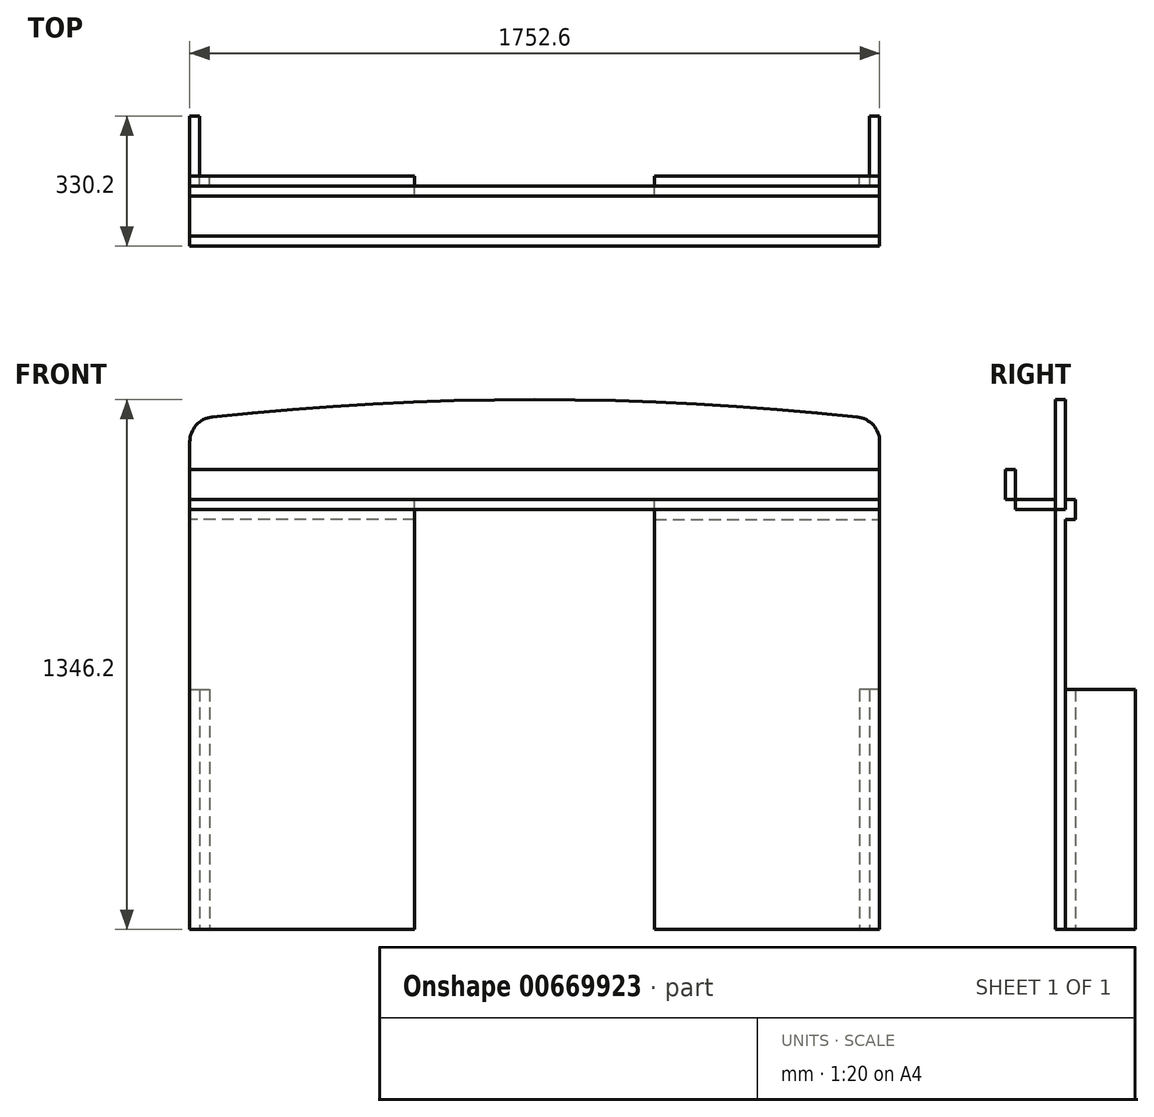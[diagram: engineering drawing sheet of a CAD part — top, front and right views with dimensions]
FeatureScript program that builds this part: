
annotation { "Feature Type Name" : "Feature", "Feature Type Description" : "" }
export const myFeature = defineFeature(function(context is Context, id is Id, definition is map)
    precondition{}
    {
        {
            var Q0;
            Q0=qCreatedBy(makeId("Top.planeOp"),FACE);
            var sketch = newSketch(context, id + "F0", { "sketchPlane" : qUnion([Q0])});
            skLineSegment(sketch, "E0.bottom", {"start": v(-876.3, 38.1) * mm, "end": v(876.3, 38.1) * mm, "construction": true});
            skLineSegment(sketch, "E0.top", {"start": v(-876.3, -38.1) * mm, "end": v(876.3, -38.1) * mm, "construction": true});
            skLineSegment(sketch, "E0.left", {"start": v(-876.3, 38.1) * mm, "end": v(-876.3, -38.1) * mm, "construction": true});
            skLineSegment(sketch, "E0.right", {"start": v(876.3, 38.1) * mm, "end": v(876.3, -38.1) * mm, "construction": true});
            skPoint(sketch, "E0.middle", {"position": v(0, 0) * mm});
            skLineSegment(sketch, "E1.bottom", {"start": v(-876.3, 38.1) * mm, "end": v(-850.9, 38.1) * mm});
            skLineSegment(sketch, "E1.top", {"start": v(-876.3, -139.7) * mm, "end": v(-850.9, -139.7) * mm});
            skLineSegment(sketch, "E1.left", {"start": v(-876.3, 38.1) * mm, "end": v(-876.3, -139.7) * mm});
            skLineSegment(sketch, "E1.right", {"start": v(-850.9, 38.1) * mm, "end": v(-850.9, -139.7) * mm});
            skSolve(sketch);
        }
        {
            var Q0;
            Q0 = qSketchRegion(id + "F0", true);
            extrude(context, id + "F1", {"entities" : qUnion([Q0]), "depth" : 609.6 * mm, "offsetDistance" : 25.4 * mm});
        }
        {
            var Q0;
            Q0=qCreatedBy(makeId("Top.planeOp"),FACE);
            var sketch = newSketch(context, id + "F2", { "sketchPlane" : qUnion([Q0])});
            skLineSegment(sketch, "E2.bottom", {"start": v(-850.9, -139.7) * mm, "end": v(-825.5, -139.7) * mm});
            skLineSegment(sketch, "E2.top", {"start": v(-850.9, -114.3) * mm, "end": v(-825.5, -114.3) * mm});
            skLineSegment(sketch, "E2.left", {"start": v(-850.9, -139.7) * mm, "end": v(-850.9, -114.3) * mm});
            skLineSegment(sketch, "E2.right", {"start": v(-825.5, -139.7) * mm, "end": v(-825.5, -114.3) * mm});
            skSolve(sketch);
        }
        {
            var Q0;
            Q0 = qSketchRegion(id + "F2", true);
            extrude(context, id + "F3", {"entities" : qUnion([Q0]), "depth" : 609.6 * mm, "offsetDistance" : 25.4 * mm});
        }
        {
            var Q0;
            Q0=makeQuery(id+"F1.opExtrude","SWEPT_FACE",FACE,{"disambiguationData":[OSD([sQuery(id+"F0.wireOp",EDGE,"E1.top")])]});
            var sketch = newSketch(context, id + "F4", { "sketchPlane" : qUnion([Q0])});
            skLineSegment(sketch, "E3", {"start": v(-876.3, 0) * mm, "end": v(-876.3, 1066.8) * mm});
            skLineSegment(sketch, "E4", {"start": v(-304.8, 1066.8) * mm, "end": v(-304.8, 0) * mm});
            skLineSegment(sketch, "E5", {"start": v(-304.8, 0) * mm, "end": v(-876.3, 0) * mm});
            skLineSegment(sketch, "E6", {"start": v(-876.3, 1066.8) * mm, "end": v(-304.8, 1066.8) * mm});
            skSolve(sketch);
        }
        {
            var Q0;
            Q0 = qSketchRegion(id + "F4", true);
            extrude(context, id + "F5", {"entities" : qUnion([Q0]), "depth" : 25.4 * mm, "offsetDistance" : 25.4 * mm});
        }
        {
            var Q0;
            Q0=makeQuery(id+"F5.opExtrude","CAP_FACE",FACE,{"disambiguationData":[OSD([sQuery(id+"F4.wireOp",EDGE,"E3"),sQuery(id+"F4.wireOp",EDGE,"E4"),sQuery(id+"F4.wireOp",EDGE,"E5"),sQuery(id+"F4.wireOp",EDGE,"E6")])],"isStart":true});
            var sketch = newSketch(context, id + "F6", { "sketchPlane" : qUnion([Q0])});
            skLineSegment(sketch, "E7", {"start": v(876.3, 1066.8) * mm, "end": v(876.3, 1295.4) * mm});
            skLineSegment(sketch, "E8", {"start": v(0, 0) * mm, "end": v(0, 1346.2) * mm, "construction": true});
            skArc(sketch, "E9", {"start": v(876.3, 1295.4) * mm, "mid": v(438.89, 1333.49) * mm, "end": v(0, 1346.2) * mm});
            skLineSegment(sketch, "E10", {"start": v(0, 1346.2) * mm, "end": v(-1371.48, 1346.2) * mm, "construction": true});
            skLineSegment(sketch, "E11", {"start": v(0, 1066.8) * mm, "end": v(0, 1346.2) * mm});
            skLineSegment(sketch, "E12", {"start": v(0, 1066.8) * mm, "end": v(304.8, 1066.8) * mm});
            skSolve(sketch);
        }
        {
            var Q0;
            Q0 = qSketchRegion(id + "F6", true);
            var Q1;
            Q1=makeQuery(id+"F6.imprint","IMPRINT",FACE,{"disambiguationData":[TD([[makeQuery(id+"F6.imprint","IMPRINT",EDGE,{"derivedFrom":sQuery(id+"F6.wireOp",EDGE,"E7")}),1.0]])]});
            extrude(context, id + "F7", {"entities" : qUnion([Q0, Q1]), "oppositeDirection" : true, "depth" : 25.4 * mm, "offsetDistance" : 25.4 * mm});
        }
        {
            var Q0;
            Q0=makeQuery(id+"F7.opExtrude","CAP_FACE",FACE,{"disambiguationData":[OSD([sQuery(id+"F4.wireOp",EDGE,"E6"),sQuery(id+"F6.wireOp",EDGE,"E7"),sQuery(id+"F6.wireOp",EDGE,"E9"),sQuery(id+"F6.wireOp",EDGE,"E11"),sQuery(id+"F6.wireOp",EDGE,"E12")])],"isStart":true});
            var sketch = newSketch(context, id + "F8", { "sketchPlane" : qUnion([Q0])});
            skLineSegment(sketch, "E13.bottom", {"start": v(304.8, 1041.4) * mm, "end": v(876.3, 1041.4) * mm});
            skLineSegment(sketch, "E13.top", {"start": v(304.8, 1092.2) * mm, "end": v(876.3, 1092.2) * mm});
            skLineSegment(sketch, "E13.left", {"start": v(304.8, 1041.4) * mm, "end": v(304.8, 1092.2) * mm});
            skLineSegment(sketch, "E13.right", {"start": v(876.3, 1041.4) * mm, "end": v(876.3, 1092.2) * mm});
            skPoint(sketch, "E13.middle", {"position": v(590.55, 1066.8) * mm});
            skSolve(sketch);
        }
        {
            var Q0;
            {var subQ0=sQuery(id+"F8.wireOp",EDGE,"E13.top");Q0=makeQuery(id+"F8.imprint","IMPRINT",FACE,{"disambiguationData":[TD([[makeQuery(id+"F8.imprint","IMPRINT",EDGE,{"derivedFrom":subQ0}),-1.0]])]});}
            var Q1;
            {var subQ0=sQuery(id+"F8.wireOp",EDGE,"E13.bottom");Q1=makeQuery(id+"F8.imprint","IMPRINT",FACE,{"disambiguationData":[TD([[makeQuery(id+"F8.imprint","IMPRINT",EDGE,{"derivedFrom":subQ0}),1.0]])]});}
            extrude(context, id + "F9", {"entities" : qUnion([Q0, Q1]), "depth" : 25.4 * mm, "offsetDistance" : 25.4 * mm});
        }
        {
            var Q0;
            Q0=makeQuery(id+"F7.opExtrude","SWEPT_BODY",BODY,{"disambiguationData":[OSD([sQuery(id+"F4.wireOp",EDGE,"E6"),sQuery(id+"F6.wireOp",EDGE,"E7"),sQuery(id+"F6.wireOp",EDGE,"E9"),sQuery(id+"F6.wireOp",EDGE,"E11"),sQuery(id+"F6.wireOp",EDGE,"E12")])]});
            var Q1;
            Q1=qCreatedBy(makeId("Right.planeOp"),FACE);
            mirror(context, id + "F10", {"operationType" : NewBodyOperationType.ADD, "entities" : qUnion([Q0]), "mirrorPlane" : qUnion([Q1])});
        }
        {
            var Q0;
            Q0=makeQuery(id+"F9.opExtrude","SWEPT_BODY",BODY,{"disambiguationData":[OSD([sQuery(id+"F8.wireOp",EDGE,"E13.bottom"),sQuery(id+"F8.wireOp",EDGE,"E13.top"),sQuery(id+"F8.wireOp",EDGE,"E13.left"),sQuery(id+"F8.wireOp",EDGE,"E13.right")])]});
            var Q1;
            Q1=makeQuery(id+"F5.opExtrude","SWEPT_BODY",BODY,{"disambiguationData":[OSD([sQuery(id+"F4.wireOp",EDGE,"E3"),sQuery(id+"F4.wireOp",EDGE,"E4"),sQuery(id+"F4.wireOp",EDGE,"E5"),sQuery(id+"F4.wireOp",EDGE,"E6")])]});
            var Q2;
            Q2=makeQuery(id+"F3.opExtrude","SWEPT_BODY",BODY,{"disambiguationData":[OSD([sQuery(id+"F2.wireOp",EDGE,"E2.bottom"),sQuery(id+"F2.wireOp",EDGE,"E2.top"),sQuery(id+"F2.wireOp",EDGE,"E2.left"),sQuery(id+"F2.wireOp",EDGE,"E2.right")])]});
            var Q3;
            Q3=makeQuery(id+"F1.opExtrude","SWEPT_BODY",BODY,{"disambiguationData":[OSD([sQuery(id+"F0.wireOp",EDGE,"E1.bottom"),sQuery(id+"F0.wireOp",EDGE,"E1.top"),sQuery(id+"F0.wireOp",EDGE,"E1.left"),sQuery(id+"F0.wireOp",EDGE,"E1.right")])]});
            var Q4;
            Q4=makeQuery(id+"F7.opExtrude","SWEPT_BODY",BODY,{"disambiguationData":[OSD([sQuery(id+"F4.wireOp",EDGE,"E6"),sQuery(id+"F6.wireOp",EDGE,"E7"),sQuery(id+"F6.wireOp",EDGE,"E9"),sQuery(id+"F6.wireOp",EDGE,"E11"),sQuery(id+"F6.wireOp",EDGE,"E12")])]});
            var Q5;
            Q5=qCreatedBy(makeId("Right.planeOp"),FACE);
            mirror(context, id + "F11", {"entities" : qUnion([Q0, Q1, Q2, Q3, Q4]), "mirrorPlane" : qUnion([Q5])});
        }
        {
            var Q0;
            Q0=makeQuery(id+"F7.opExtrude","SWEPT_EDGE",EDGE,{"disambiguationData":[OSD([sQuery(id+"F6.wireOp",EDGE,"E7"),sQuery(id+"F6.wireOp",EDGE,"E9")])]});
            var Q1;
            Q1=makeQuery(id+"F10.opPattern","COPY",EDGE,{"derivedFrom":makeQuery(id+"F7.opExtrude","SWEPT_EDGE",EDGE,{"disambiguationData":[OSD([sQuery(id+"F6.wireOp",EDGE,"E7"),sQuery(id+"F6.wireOp",EDGE,"E9")])]}),"instanceName":"1"});
            var Q2;
            Q2=makeQuery(id+"F11.opPattern","COPY",EDGE,{"derivedFrom":makeQuery(id+"F10.opPattern","COPY",EDGE,{"derivedFrom":makeQuery(id+"F7.opExtrude","SWEPT_EDGE",EDGE,{"disambiguationData":[OSD([sQuery(id+"F6.wireOp",EDGE,"E7"),sQuery(id+"F6.wireOp",EDGE,"E9")])]}),"instanceName":"1"}),"instanceName":"1"});
            var Q3;
            Q3=makeQuery(id+"F11.opPattern","COPY",EDGE,{"derivedFrom":makeQuery(id+"F7.opExtrude","SWEPT_EDGE",EDGE,{"disambiguationData":[OSD([sQuery(id+"F6.wireOp",EDGE,"E7"),sQuery(id+"F6.wireOp",EDGE,"E9")])]}),"instanceName":"1"});
            fillet(context, id + "F12", {"entities" : qUnion([Q0, Q1, Q2, Q3]), "radius" : 63.5 * mm, "tangentPropagation" : true, "allowEdgeOverflow" : false});
        }
        {
            var Q0;
            {var subQ0=makeQuery(id+"F7.opExtrude","CAP_FACE",FACE,{"disambiguationData":[OSD([sQuery(id+"F4.wireOp",EDGE,"E6"),sQuery(id+"F6.wireOp",EDGE,"E7"),sQuery(id+"F6.wireOp",EDGE,"E9"),sQuery(id+"F6.wireOp",EDGE,"E11"),sQuery(id+"F6.wireOp",EDGE,"E12")])],"isStart":false});Q0=makeQuery(id+"F10.boolean.opBoolean","MERGE",FACE,{"derivedFrom":[subQ0,makeQuery(id+"F10.opPattern","COPY",FACE,{"derivedFrom":subQ0,"instanceName":"1"})]});}
            var sketch = newSketch(context, id + "F13", { "sketchPlane" : qUnion([Q0])});
            skLineSegment(sketch, "E14.bottom", {"start": v(-876.3, 1066.8) * mm, "end": v(876.3, 1066.8) * mm});
            skLineSegment(sketch, "E14.top", {"start": v(-876.3, 1092.2) * mm, "end": v(876.3, 1092.2) * mm});
            skLineSegment(sketch, "E14.left", {"start": v(-876.3, 1066.8) * mm, "end": v(-876.3, 1092.2) * mm});
            skLineSegment(sketch, "E14.right", {"start": v(876.3, 1066.8) * mm, "end": v(876.3, 1092.2) * mm});
            skSolve(sketch);
        }
        {
            var Q0;
            Q0 = qSketchRegion(id + "F13", true);
            extrude(context, id + "F14", {"entities" : qUnion([Q0]), "depth" : 101.6 * mm, "offsetDistance" : 25.4 * mm});
        }
        {
            var Q0;
            Q0=makeQuery(id+"F14.opExtrude","CAP_FACE",FACE,{"disambiguationData":[OSD([sQuery(id+"F13.wireOp",EDGE,"E14.bottom"),sQuery(id+"F13.wireOp",EDGE,"E14.top"),sQuery(id+"F13.wireOp",EDGE,"E14.left"),sQuery(id+"F13.wireOp",EDGE,"E14.right")])],"isStart":false});
            var sketch = newSketch(context, id + "F15", { "sketchPlane" : qUnion([Q0])});
            skLineSegment(sketch, "E15.bottom", {"start": v(-876.3, 1066.8) * mm, "end": v(876.3, 1066.8) * mm});
            skLineSegment(sketch, "E15.top", {"start": v(-876.3, 1168.4) * mm, "end": v(876.3, 1168.4) * mm});
            skLineSegment(sketch, "E15.left", {"start": v(-876.3, 1066.8) * mm, "end": v(-876.3, 1168.4) * mm});
            skLineSegment(sketch, "E15.right", {"start": v(876.3, 1066.8) * mm, "end": v(876.3, 1168.4) * mm});
            skSolve(sketch);
        }
        {
            var Q0;
            {var subQ0=sQuery(id+"F15.wireOp",EDGE,"E15.top");Q0=makeQuery(id+"F15.imprint","IMPRINT",FACE,{"disambiguationData":[TD([[makeQuery(id+"F15.imprint","IMPRINT",EDGE,{"derivedFrom":subQ0}),-1.0]])]});}
            var Q1;
            {var subQ0=sQuery(id+"F15.wireOp",EDGE,"E15.bottom");Q1=makeQuery(id+"F15.imprint","IMPRINT",FACE,{"disambiguationData":[TD([[makeQuery(id+"F15.imprint","IMPRINT",EDGE,{"derivedFrom":subQ0}),-1.0]])]});}
            extrude(context, id + "F16", {"entities" : qUnion([Q0, Q1]), "depth" : 25.4 * mm, "offsetDistance" : 25.4 * mm});
        }
    });
